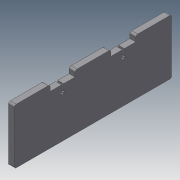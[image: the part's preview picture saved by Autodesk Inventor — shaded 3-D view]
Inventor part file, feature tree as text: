
AUTODESK INVENTOR PART (.ipt)
format: ipt  version: 2014 (Build 180170000, 170)  size: 150,016 bytes
history: native  units: mm
features: extrude x3, sketch x3, mirror x1, fillet x1
ambient origin geometry x8: Origin, YZ Plane, XZ Plane, XY Plane, X Axis, Y Axis, Z Axis, Center Point
bodies: Solid1 (feature_tree)
feature tree (8):
  extrude  "Extrusion1"  Depth=50.0mm
  extrude  "Extrusion2"  Depth=6.0mm
  extrude  "Extrusion3"  Depth=25.25mm
  mirror  "Mirror1"
  fillet  "Fillet1"  Radius=6.0mm
  sketch  "Sketch1"  dims[d0=160.0mm d1=50.0mm]
  sketch  "Sketch2"  dims[d2=6.0mm d3=0.0mm d4=6.0mm]
  sketch  "Sketch3"  dims[d5=25.25mm d6=25.25mm d7=6.0mm d8=0.0mm d9=1.8mm d10=4.1mm d11=2.1mm d12=1.05mm d13=9.0mm d14=2.05mm d15=6.0mm d16=6.0mm d17=0.0mm d18=2.0mm]
